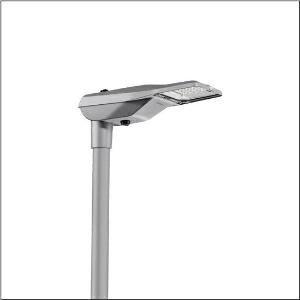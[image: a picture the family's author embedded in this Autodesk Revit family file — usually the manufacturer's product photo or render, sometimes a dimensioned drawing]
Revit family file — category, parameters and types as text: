
# Revit family: streetlight_sl_21_micro___st1_5a_5xe1p33t08db_27e3
name_source: partatom
category: Lighting Fixtures
units: mm (PartAtom-declared; Revit-internal decimal feet)

## family parameters
Cut with Voids When Loaded = No
Host = Face
Light Source = No
Part Type = Normal
Room Calculation Point = No
Round Connector Dimension = Use Diameter
Shared = No

## types (1)
- --- (1 x LED, 5020 lm, 39.1 W, 3000K)
    Apparent Load = 39 VA
    CIE Flux Codes = 22 53 95 100 100
    Color Rendering = 70
    Color Temperature = 3000K
    Default Elevation = 1800 mm
    Description = Streetlight SL 21 micro, mast luminaire, primary light control with lens, of PMMA, primary optical cover: cover, of toughened safety glass, transparent, light distribution: ST1.5a, light emission: direct distribution, primary light characteristic: asymmetric, installation type: side-entry, post-top, LED, High Power LED, rated luminous flux: 5.020lm, luminous efficacy: 128lm/W, light colour: 730, colour temperature: 3000K, control: flexible luminous flux parameterisation, time-dependent luminous flux control, constant luminous flux control, overheat protection, presetting dimming logarithmic, mains connection: 220..240V, AC, 50/60Hz, start of lifetime: 39W, end of service life: 41W, reduction: 18W, luminaire housing, of diecast aluminium, powder-coated, Siteco® metallic grey (DB 702S), corrosivity category C5 mid according to DIN EN ISO 12944, please order mast flange separately, inclination adjustable: 0°, 5°, 10°, 15°, sealing non-destructively replaceable, multi-level sealing system, length: 528mm, width: 235mm, height: 110mm, mast flange for spigot size: 42mm (side-entry): 5XC10008XM4, 60/48mm (side-entry/post-top): 5XC10108XM2, 76/60mm (side-entry/post-top): 5XC10108XM1, Smart Interface below and above, protection rating (complete): IP66, insulation class (complete): insulation class II (safety insulation), certification: CE, ENEC, ENEC+, VDE, impact resistance: IK09, permissible operating ambient temperature for outdoor applications: -40..+50°C, standard-compliant lighting for roads and squares, packaging unit: 1 piece

Light Distribution: ST1.5a
    Height = 110 mm
    Lamp = 1 x LED
    Lamp Light Flux = 5020 lm
    Lamp Power = 39.1 W
    Lamp count = 1
    Length = 528 mm
    Luminous efficacy = 128 lm/W
    Manufacturer = Siteco
    ModVariant = No
    Model = 5XE1P33T08DB
    Number of Poles = 1
    OnlyDefault = Yes
    Power Factor = 1
    Product Name = Streetlight SL 21 micro | ST1.5a
    Product group = mast luminaire | pylon top
    ProductGroupID = 6100
    Protection Class = Protection class II
    Protection Degree = IP 66
    RLX_Detail_Level = 1
    RLX_Emergency_Light_Flux = 0 lm
    RLX_Emergency_Type = 0
    RLX_Emergency_Type_DB = No
    RlxData = <blob elided: 102469 chars, md5=9ae730f2>
    Socket = socket
    Standby Power = 0 W
    System Light Flux = 5020 lm
    System Power = 39 W
    Type Comments = factory setting: luminous flux: 100 % | dim-lin: 254 | 765 mA
    Type Image = l_1007239.jpg
    URL = http://relux.com
    VarID = @adj_103829
    Voltage = 0 V
    Weight = 0.00 kg
    Width = 235 mm

## geometry (parser evidence)
native form markers: Blend x4, Sweep x12
no freeform markers — native parametric forms only
